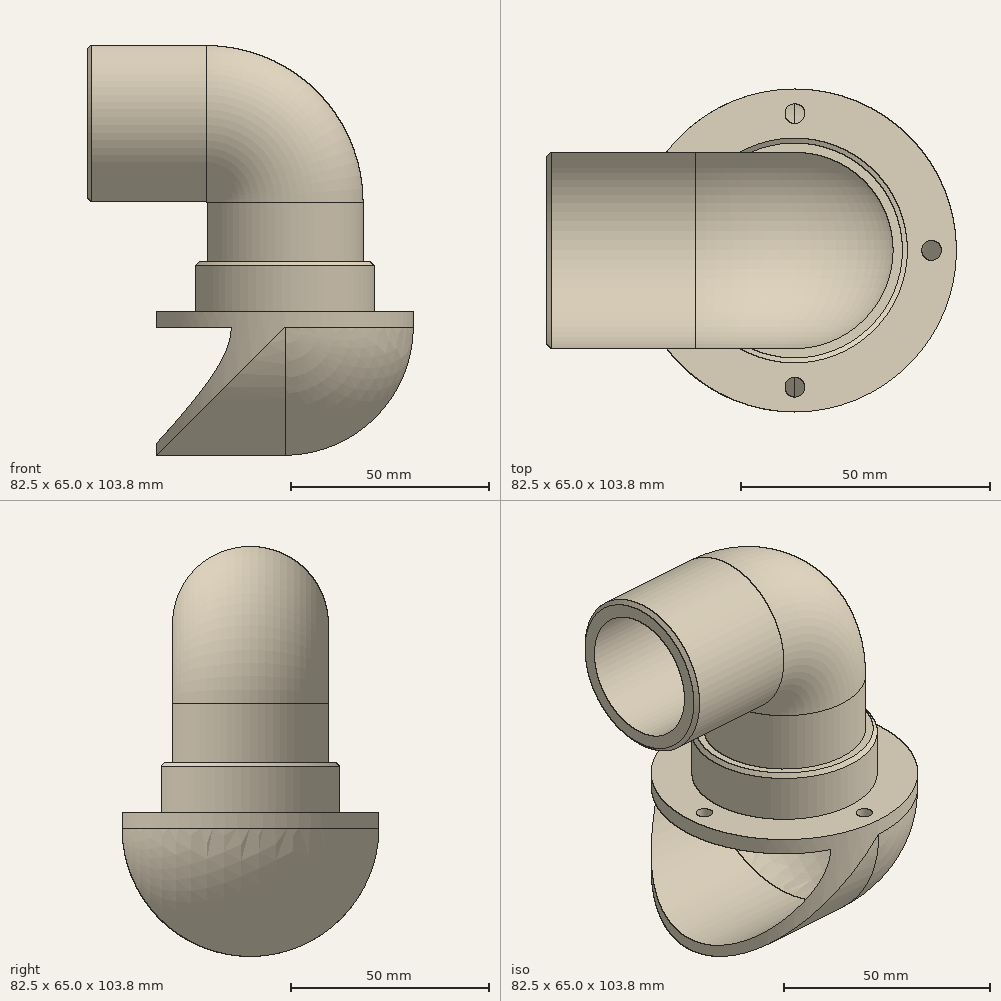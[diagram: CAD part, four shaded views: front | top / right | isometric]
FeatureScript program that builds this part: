
annotation { "Feature Type Name" : "Feature", "Feature Type Description" : "" }
export const myFeature = defineFeature(function(context is Context, id is Id, definition is map)
    precondition{}
    {
        {
            var Q0;
            Q0=qCreatedBy(makeId("Top.planeOp"),FACE);
            var sketch = newSketch(context, id + "F0", { "sketchPlane" : qUnion([Q0])});
            skCircle(sketch, "E0", {"center": v(0, 0) * mm, "radius": 32.5 * mm});
            skSolve(sketch);
        }
        {
            var Q0;
            Q0=qSketchRegion(id+"F0",true);
            extrude(context, id + "F1", {"entities" : qUnion([Q0]), "depth" : 4 * mm, "offsetDistance" : 25 * mm});
        }
        {
            var Q0;
            Q0=makeQuery(id+"F1.opExtrude","CAP_FACE",FACE,{"disambiguationData":[OSD([sQuery(id+"F0.wireOp",EDGE,"E0")])],"isStart":false});
            var sketch = newSketch(context, id + "F2", { "sketchPlane" : qUnion([Q0])});
            skCircle(sketch, "E1", {"center": v(0, 0) * mm, "radius": 22.62 * mm});
            skSolve(sketch);
        }
        {
            var Q0;
            Q0=qSketchRegion(id+"F2",true);
            extrude(context, id + "F3", {"entities" : qUnion([Q0]), "operationType" : NewBodyOperationType.ADD, "depth" : 12.5 * mm, "offsetDistance" : 25 * mm});
        }
        {
            var Q0;
            Q0=makeQuery(id+"F3.opExtrude","CAP_FACE",FACE,{"disambiguationData":[OSD([sQuery(id+"F2.wireOp",EDGE,"E1")])],"isStart":false});
            var sketch = newSketch(context, id + "F4", { "sketchPlane" : qUnion([Q0])});
            skCircle(sketch, "E2", {"center": v(0, 0) * mm, "radius": 19.75 * mm});
            skSolve(sketch);
        }
        {
            var Q0;
            Q0=qSketchRegion(id+"F4",true);
            extrude(context, id + "F5", {"entities" : qUnion([Q0]), "operationType" : NewBodyOperationType.ADD, "depth" : 15 * mm, "offsetDistance" : 25 * mm});
        }
        {
            var Q0;
            Q0=makeQuery(id+"F5.opExtrude","CAP_FACE",FACE,{"disambiguationData":[OSD([sQuery(id+"F4.wireOp",EDGE,"E2")])],"isStart":false});
            var sketch = newSketch(context, id + "F6", { "sketchPlane" : qUnion([Q0])});
            skCircle(sketch, "E3", {"center": v(0, 0) * mm, "radius": 15.5 * mm});
            skSolve(sketch);
        }
        {
            var Q0;
            Q0=qSketchRegion(id+"F6",true);
            extrude(context, id + "F7", {"entities" : qUnion([Q0]), "operationType" : NewBodyOperationType.REMOVE, "endBound" : BoundingType.THROUGH_ALL, "oppositeDirection" : true, "depth" : 25 * mm, "offsetDistance" : 25 * mm});
        }
        {
            var Q0;
            Q0=makeQuery(id+"F1.opExtrude","CAP_FACE",FACE,{"disambiguationData":[OSD([sQuery(id+"F0.wireOp",EDGE,"E0")])],"isStart":false});
            var sketch = newSketch(context, id + "F8", { "sketchPlane" : qUnion([Q0])});
            skLineSegment(sketch, "E4", {"start": v(0, 39.84) * mm, "end": v(0, -38.09) * mm, "construction": true});
            skLineSegment(sketch, "E5", {"start": v(-48.97, 0) * mm, "end": v(51.42, 0) * mm, "construction": true});
            skCircle(sketch, "E6", {"center": v(0, 0) * mm, "radius": 27.5 * mm, "construction": true});
            skCircle(sketch, "E7", {"center": v(0, 27.5) * mm, "radius": 2 * mm});
            skCircle(sketch, "E8", {"center": v(27.5, 0) * mm, "radius": 2 * mm});
            skCircle(sketch, "E9", {"center": v(0, -27.5) * mm, "radius": 2 * mm});
            skCircle(sketch, "E10", {"center": v(-27.5, 0) * mm, "radius": 2 * mm});
            skSolve(sketch);
        }
        {
            var Q0;
            Q0=qSketchRegion(id+"F8",true);
            extrude(context, id + "F9", {"entities" : qUnion([Q0]), "operationType" : NewBodyOperationType.REMOVE, "endBound" : BoundingType.THROUGH_ALL, "oppositeDirection" : true, "depth" : 25 * mm, "offsetDistance" : 25 * mm});
        }
        {
            var Q0;
            Q0=makeQuery(id+"F3.opExtrude","CAP_EDGE",EDGE,{"disambiguationData":[OSD([sQuery(id+"F2.wireOp",EDGE,"E1")])],"isStart":false});
            chamfer(context, id + "F10", {"entities" : qUnion([Q0]), "width" : 1 * mm, "tangentPropagation" : true});
        }
        {
            var Q0;
            Q0=qCreatedBy(makeId("Front.planeOp"),FACE);
            var sketch = newSketch(context, id + "F11", { "sketchPlane" : qUnion([Q0])});
            skLineSegment(sketch, "E11.0", {"start": v(-19.75, 31.5) * mm, "end": v(19.75, 31.5) * mm, "construction": true});
            skLineSegment(sketch, "E12", {"start": v(0, 31.5) * mm, "end": v(0, 31.5) * mm});
            skPoint(sketch, "E13.start.orphan", {"position": v(0, 42.95) * mm});
            skArc(sketch, "E14", {"start": v(0, 31.5) * mm, "mid": v(-5.86, 45.64) * mm, "end": v(-20, 51.5) * mm});
            skLineSegment(sketch, "E15", {"start": v(-20, 51.5) * mm, "end": v(-50, 51.5) * mm});
            skSolve(sketch);
        }
        {
            var Q0;
            Q0=makeQuery(id+"F5.opExtrude","CAP_FACE",FACE,{"disambiguationData":[OSD([sQuery(id+"F4.wireOp",EDGE,"E2")])],"isStart":false});
            var sketch = newSketch(context, id + "F12", { "sketchPlane" : qUnion([Q0])});
            skCircle(sketch, "E16.0", {"center": v(0, 0) * mm, "radius": 15.5 * mm});
            skCircle(sketch, "E17.0", {"center": v(0, 0) * mm, "radius": 19.75 * mm});
            skSolve(sketch);
        }
        {
            var Q0;
            Q0=makeQuery(id+"F12.imprint","IMPRINT",FACE,{"disambiguationData":[TD([[makeQuery(id+"F12.imprint","IMPRINT",EDGE,{"derivedFrom":sQuery(id+"F12.wireOp",EDGE,"E16.0")}),-1.0]])]});
            var Q1;
            Q1 = qConstructionFilter(qBodyType(qCreatedBy(id + "F11" ,EDGE), BodyType.WIRE), ConstructionObject.NO);
            sweep(context, id + "F13", {"operationType" : NewBodyOperationType.ADD, "profiles" : qUnion([Q0]), "path" : qUnion([Q1])});
        }
        {
            var Q0;
            Q0=makeQuery(id+"F13.opSweep","CAP_EDGE",EDGE,{"disambiguationData":[OSD([sQuery(id+"F11.wireOp",VERTEX,"E15.end"),sQuery(id+"F12.wireOp",EDGE,"E17.0")])],"isStart":false});
            chamfer(context, id + "F14", {"entities" : qUnion([Q0]), "width" : 1 * mm, "tangentPropagation" : true});
        }
        {
            var Q0;
            Q0=makeQuery(id+"F1.opExtrude","CAP_FACE",FACE,{"disambiguationData":[OSD([sQuery(id+"F0.wireOp",EDGE,"E0")])],"isStart":true});
            var sketch = newSketch(context, id + "F15", { "sketchPlane" : qUnion([Q0])});
            skPoint(sketch, "E18.end.orphan", {"position": v(0, 23.15) * mm});
            skArc(sketch, "E19", {"start": v(0, -29.5) * mm, "mid": v(29.5, 0) * mm, "end": v(0, 29.5) * mm});
            skArc(sketch, "E20.0", {"start": v(0, -32.5) * mm, "mid": v(32.5, 0) * mm, "end": v(0, 32.5) * mm});
            skLineSegment(sketch, "E21", {"start": v(0, 29.5) * mm, "end": v(0, 32.5) * mm});
            skLineSegment(sketch, "E22", {"start": v(0, 32.5) * mm, "end": v(0, 29.5) * mm});
            skLineSegment(sketch, "E23", {"start": v(0, -32.5) * mm, "end": v(0, -29.5) * mm});
            skLineSegment(sketch, "E24.trimOffspring", {"start": v(0, -29.5) * mm, "end": v(0, -32.5) * mm});
            skSolve(sketch);
        }
        {
            var Q0;
            Q0=makeQuery(id+"F15.imprint","IMPRINT",FACE,{"disambiguationData":[TD([[makeQuery(id+"F15.imprint","IMPRINT",EDGE,{"derivedFrom":sQuery(id+"F15.wireOp",EDGE,"E20.0")}),-1.0]])]});
            var Q1;
            Q1=sQuery(id+"F15.wireOp",EDGE,"E22");
            revolve(context, id + "F16", {"operationType" : NewBodyOperationType.ADD, "surfaceOperationType" : NewSurfaceOperationType.NEW, "entities" : qUnion([Q0]), "axis" : qUnion([Q1]), "revolveType" : RevolveType.ONE_DIRECTION, "angle" : 90 * degree});
        }
        {
            var Q0;
            Q0=makeQuery(id+"F16.opRevolve","CAP_FACE",FACE,{"disambiguationData":[OSD([sQuery(id+"F15.wireOp",EDGE,"E19"),sQuery(id+"F15.wireOp",EDGE,"E20.0"),sQuery(id+"F15.wireOp",EDGE,"E22"),sQuery(id+"F15.wireOp",EDGE,"E24.trimOffspring")])],"isStart":false});
            var sketch = newSketch(context, id + "F17", { "sketchPlane" : qUnion([Q0])});
            skArc(sketch, "E25.0", {"start": v(-29.5, 0) * mm, "mid": v(0, -29.5) * mm, "end": v(29.5, 0) * mm});
            skArc(sketch, "E26.0", {"start": v(32.5, 0) * mm, "mid": v(0, -32.5) * mm, "end": v(-32.5, 0) * mm});
            skLineSegment(sketch, "E27.0", {"start": v(32.5, 0) * mm, "end": v(29.5, 0) * mm});
            skLineSegment(sketch, "E28.0", {"start": v(-29.5, 0) * mm, "end": v(-32.5, 0) * mm});
            skSolve(sketch);
        }
        {
            var Q0;
            Q0 = qSketchRegion(id + "F17", true);
            var Q1;
            Q1=makeQuery(id+"F1.opExtrude","SWEPT_FACE",FACE,{"disambiguationData":[OSD([sQuery(id+"F0.wireOp",EDGE,"E0")])]});
            extrude(context, id + "F18", {"entities" : qUnion([Q0]), "operationType" : NewBodyOperationType.ADD, "endBound" : BoundingType.UP_TO_SURFACE, "depth" : 25 * mm, "endBoundEntityFace" : qUnion([Q1]), "offsetDistance" : 25 * mm});
        }
    });
